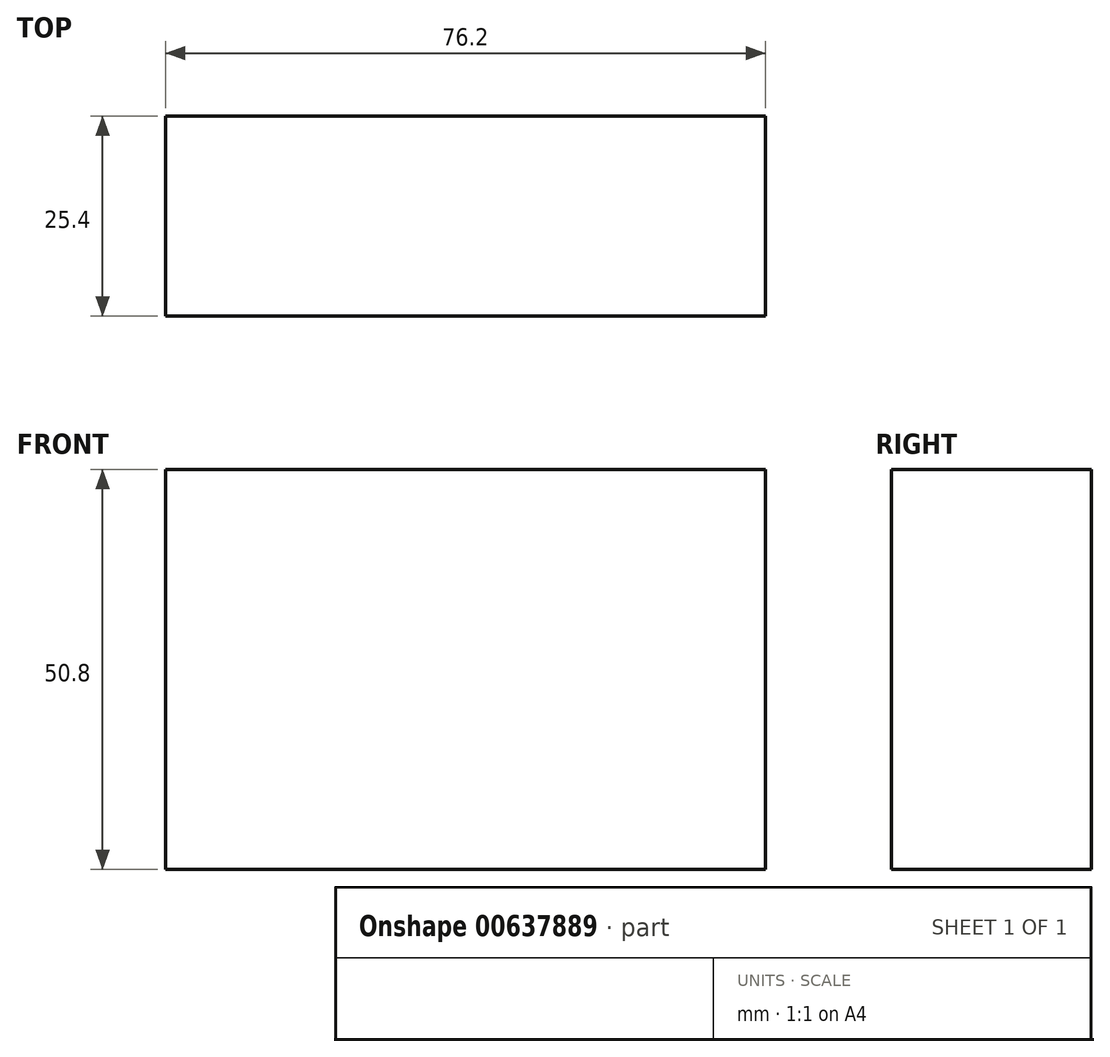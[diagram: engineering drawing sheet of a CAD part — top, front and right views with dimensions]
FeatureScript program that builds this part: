
annotation { "Feature Type Name" : "Feature", "Feature Type Description" : "" }
export const myFeature = defineFeature(function(context is Context, id is Id, definition is map)
    precondition{}
    {
        {
            var Q0;
            Q0=qCreatedBy(makeId("Front.planeOp"),FACE);
            var sketch = newSketch(context, id + "F0", { "sketchPlane" : qUnion([Q0])});
            skLineSegment(sketch, "E0.bottom", {"start": v(0, 0) * mm, "end": v(76.2, 0) * mm});
            skLineSegment(sketch, "E0.top", {"start": v(0, 50.8) * mm, "end": v(76.2, 50.8) * mm});
            skLineSegment(sketch, "E0.left", {"start": v(0, 0) * mm, "end": v(0, 50.8) * mm});
            skLineSegment(sketch, "E0.right", {"start": v(76.2, 0) * mm, "end": v(76.2, 50.8) * mm});
            skSolve(sketch);
        }
        {
            var Q0;
            Q0 = qSketchRegion(id + "F0", true);
            extrude(context, id + "F1", {"entities" : qUnion([Q0]), "depth" : 25.4 * mm, "offsetDistance" : 25.4 * mm});
        }
    });
